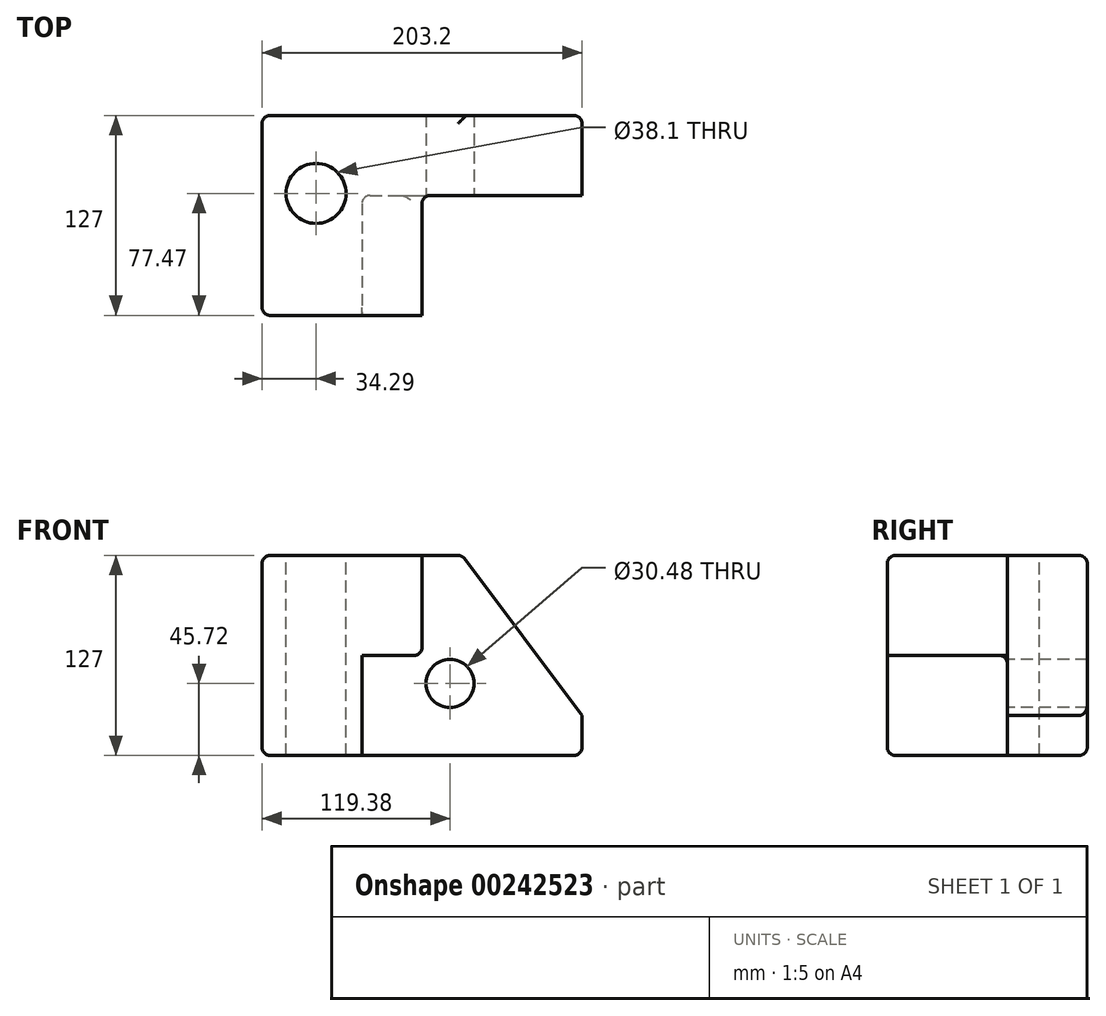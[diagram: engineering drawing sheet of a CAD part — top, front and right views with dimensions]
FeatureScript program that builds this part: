
annotation { "Feature Type Name" : "Feature", "Feature Type Description" : "" }
export const myFeature = defineFeature(function(context is Context, id is Id, definition is map)
    precondition{}
    {
        {
            var Q0;
            Q0=qCreatedBy(makeId("Front.planeOp"),FACE);
            var sketch = newSketch(context, id + "F0", { "sketchPlane" : qUnion([Q0])});
            skLineSegment(sketch, "E0.bottom", {"start": v(-101.6, 63.5) * mm, "end": v(101.6, 63.5) * mm});
            skLineSegment(sketch, "E0.top", {"start": v(-101.6, -63.5) * mm, "end": v(101.6, -63.5) * mm});
            skLineSegment(sketch, "E0.left", {"start": v(-101.6, 63.5) * mm, "end": v(-101.6, -63.5) * mm});
            skLineSegment(sketch, "E0.right", {"start": v(101.6, 63.5) * mm, "end": v(101.6, -63.5) * mm});
            skPoint(sketch, "E0.middle", {"position": v(0, 0) * mm});
            skSolve(sketch);
        }
        {
            var Q0;
            Q0=makeQuery(id+"F0.imprint","IMPRINT",FACE,{"disambiguationData":[TD([[makeQuery(id+"F0.imprint","IMPRINT",EDGE,{"derivedFrom":sQuery(id+"F0.wireOp",EDGE,"E0.bottom")}),-1.0]])]});
            extrude(context, id + "F1", {"entities" : qUnion([Q0]), "depth" : 127 * mm});
        }
        {
            var Q0;
            Q0=makeQuery(id+"F1.opExtrude","CAP_FACE",FACE,{"disambiguationData":[OSD([sQuery(id+"F0.wireOp",EDGE,"E0.bottom"),sQuery(id+"F0.wireOp",EDGE,"E0.top"),sQuery(id+"F0.wireOp",EDGE,"E0.left"),sQuery(id+"F0.wireOp",EDGE,"E0.right")])],"isStart":false});
            var sketch = newSketch(context, id + "F2", { "sketchPlane" : qUnion([Q0])});
            skLineSegment(sketch, "E1", {"start": v(-101.6, -63.5) * mm, "end": v(-38.1, -63.5) * mm});
            skLineSegment(sketch, "E2", {"start": v(-38.1, -63.5) * mm, "end": v(-38.1, 0) * mm});
            skLineSegment(sketch, "E3", {"start": v(-101.6, 63.5) * mm, "end": v(0, 63.5) * mm});
            skLineSegment(sketch, "E4", {"start": v(-38.1, 0) * mm, "end": v(0, 0) * mm});
            skLineSegment(sketch, "E5", {"start": v(0, 63.5) * mm, "end": v(0, 0) * mm});
            skLineSegment(sketch, "E6", {"start": v(-101.6, 63.5) * mm, "end": v(-101.6, -63.5) * mm});
            skSolve(sketch);
        }
        {
            var Q0;
            {var subQ3=sQuery(id+"F2.wireOp",EDGE,"E2");Q0=makeQuery(id+"F2.imprint","IMPRINT",FACE,{"disambiguationData":[TD([[makeQuery(id+"F2.imprint","IMPRINT",EDGE,{"derivedFrom":subQ3}),-1.0]])]});}
            extrude(context, id + "F3", {"entities" : qUnion([Q0]), "operationType" : NewBodyOperationType.REMOVE, "oppositeDirection" : true, "depth" : 76.2 * mm});
        }
        {
            var Q0;
            Q0=makeQuery(id+"F1.opExtrude","SWEPT_EDGE",EDGE,{"disambiguationData":[OSD([sQuery(id+"F0.wireOp",EDGE,"E0.bottom"),sQuery(id+"F0.wireOp",EDGE,"E0.right")])]});
            chamfer(context, id + "F4", {"entities" : qUnion([Q0]), "chamferType" : ChamferType.TWO_OFFSETS, "width1" : 76.2 * mm, "oppositeDirection" : false, "width2" : 101.6 * mm, "tangentPropagation" : true});
        }
        {
            var Q0;
            Q0=makeQuery(id+"F1.opExtrude","CAP_EDGE",EDGE,{"disambiguationData":[OSD([sQuery(id+"F0.wireOp",EDGE,"E0.bottom")])],"isStart":false});
            var Q1;
            Q1=makeQuery(id+"F3.boolean.opBoolean","COPY",EDGE,{"derivedFrom":makeQuery(id+"F3.opExtrude","SWEPT_EDGE",EDGE,{"disambiguationData":[OSD([sQuery(id+"F0.wireOp",EDGE,"E0.bottom"),sQuery(id+"F2.wireOp",EDGE,"E3"),sQuery(id+"F2.wireOp",EDGE,"E5")])]})});
            var Q2;
            Q2=makeQuery(id+"F3.boolean.opBoolean","COPY",EDGE,{"derivedFrom":makeQuery(id+"F3.opExtrude","CAP_EDGE",EDGE,{"disambiguationData":[OSD([sQuery(id+"F2.wireOp",EDGE,"E5")])],"isStart":true})});
            var Q3;
            Q3=makeQuery(id+"F1.opExtrude","SWEPT_EDGE",EDGE,{"disambiguationData":[OSD([sQuery(id+"F0.wireOp",EDGE,"E0.bottom"),sQuery(id+"F0.wireOp",EDGE,"E0.left")])]});
            var Q4;
            Q4=makeQuery(id+"F1.opExtrude","CAP_EDGE",EDGE,{"disambiguationData":[OSD([sQuery(id+"F0.wireOp",EDGE,"E0.bottom")])],"isStart":true});
            var Q5;
            Q5=makeQuery(id+"F3.boolean.opBoolean","COPY",EDGE,{"derivedFrom":makeQuery(id+"F3.opExtrude","CAP_EDGE",EDGE,{"disambiguationData":[OSD([sQuery(id+"F0.wireOp",EDGE,"E0.bottom")])],"isStart":false})});
            var Q6;
            {var subQ0=sQuery(id+"F0.wireOp",EDGE,"E0.bottom");Q6=makeQuery(id+"F4.opChamfer","BLEND_EDGE",EDGE,{"blendedFrom":[makeQuery(id+"F1.opExtrude","SWEPT_EDGE",EDGE,{"disambiguationData":[OSD([subQ0,sQuery(id+"F0.wireOp",EDGE,"E0.right")])]}),makeQuery(id+"F1.opExtrude","SWEPT_FACE",FACE,{"disambiguationData":[OSD([subQ0])]})],"blendedInto":[makeQuery(id+"F1.opExtrude","SWEPT_FACE",FACE,{"disambiguationData":[OSD([subQ0])]})]});}
            var Q7;
            Q7=makeQuery(id+"F3.boolean.opBoolean","COPY",EDGE,{"derivedFrom":makeQuery(id+"F3.opExtrude","CAP_EDGE",EDGE,{"disambiguationData":[OSD([sQuery(id+"F2.wireOp",EDGE,"E5")])],"isStart":false})});
            var Q8;
            Q8=makeQuery(id+"F3.boolean.opBoolean","COPY",EDGE,{"derivedFrom":makeQuery(id+"F3.opExtrude","SWEPT_EDGE",EDGE,{"disambiguationData":[OSD([sQuery(id+"F2.wireOp",EDGE,"E4"),sQuery(id+"F2.wireOp",EDGE,"E5")])]})});
            var Q9;
            Q9=makeQuery(id+"F3.boolean.opBoolean","COPY",EDGE,{"derivedFrom":makeQuery(id+"F3.opExtrude","CAP_EDGE",EDGE,{"disambiguationData":[OSD([sQuery(id+"F2.wireOp",EDGE,"E4")])],"isStart":true})});
            var Q10;
            Q10=makeQuery(id+"F3.boolean.opBoolean","COPY",EDGE,{"derivedFrom":makeQuery(id+"F3.opExtrude","CAP_EDGE",EDGE,{"disambiguationData":[OSD([sQuery(id+"F2.wireOp",EDGE,"E2")])],"isStart":true})});
            var Q11;
            Q11=makeQuery(id+"F1.opExtrude","CAP_EDGE",EDGE,{"disambiguationData":[OSD([sQuery(id+"F0.wireOp",EDGE,"E0.left")])],"isStart":false});
            var Q12;
            Q12=makeQuery(id+"F3.boolean.opBoolean","COPY",EDGE,{"derivedFrom":makeQuery(id+"F3.opExtrude","CAP_EDGE",EDGE,{"disambiguationData":[OSD([sQuery(id+"F2.wireOp",EDGE,"E2")])],"isStart":false})});
            var Q13;
            Q13=makeQuery(id+"F1.opExtrude","CAP_EDGE",EDGE,{"disambiguationData":[OSD([sQuery(id+"F0.wireOp",EDGE,"E0.top")])],"isStart":false});
            var Q14;
            Q14=makeQuery(id+"F3.boolean.opBoolean","COPY",EDGE,{"derivedFrom":makeQuery(id+"F3.opExtrude","SWEPT_EDGE",EDGE,{"disambiguationData":[OSD([sQuery(id+"F0.wireOp",EDGE,"E0.top"),sQuery(id+"F2.wireOp",EDGE,"E1"),sQuery(id+"F2.wireOp",EDGE,"E2")])]})});
            var Q15;
            Q15=makeQuery(id+"F1.opExtrude","SWEPT_EDGE",EDGE,{"disambiguationData":[OSD([sQuery(id+"F0.wireOp",EDGE,"E0.top"),sQuery(id+"F0.wireOp",EDGE,"E0.right")])]});
            fillet(context, id + "F5", {"entities" : qUnion([Q0, Q1, Q2, Q3, Q4, Q5, Q6, Q7, Q8, Q9, Q10, Q11, Q12, Q13, Q14, Q15]), "radius" : 5.08 * mm, "tangentPropagation" : true, "allowEdgeOverflow" : false});
        }
        {
            var Q0;
            Q0=makeQuery(id+"F3.boolean.opBoolean","COPY",FACE,{"derivedFrom":makeQuery(id+"F3.opExtrude","CAP_FACE",FACE,{"disambiguationData":[OSD([sQuery(id+"F0.wireOp",EDGE,"E0.bottom"),sQuery(id+"F0.wireOp",EDGE,"E0.top"),sQuery(id+"F0.wireOp",EDGE,"E0.right"),sQuery(id+"F2.wireOp",EDGE,"E2"),sQuery(id+"F2.wireOp",EDGE,"E4"),sQuery(id+"F2.wireOp",EDGE,"E5")])],"isStart":false})});
            var sketch = newSketch(context, id + "F6", { "sketchPlane" : qUnion([Q0])});
            skCircle(sketch, "E7", {"center": v(17.78, -17.78) * mm, "radius": 15.24 * mm});
            skSolve(sketch);
        }
        {
            var Q0;
            Q0=makeQuery(id+"F6.imprint","IMPRINT",FACE,{"disambiguationData":[TD([[makeQuery(id+"F6.imprint","IMPRINT",EDGE,{"derivedFrom":sQuery(id+"F6.wireOp",EDGE,"E7")}),1.0]])]});
            var Q1;
            Q1=sQuery(id+"F6.wireOp",EDGE,"E7");
            extrude(context, id + "F7", {"entities" : qUnion([Q0]), "operationType" : NewBodyOperationType.REMOVE, "surfaceEntities" : qUnion([Q1]), "oppositeDirection" : true, "depth" : 50.8 * mm});
        }
        {
            var Q0;
            Q0=makeQuery(id+"F1.opExtrude","SWEPT_FACE",FACE,{"disambiguationData":[OSD([sQuery(id+"F0.wireOp",EDGE,"E0.bottom")])]});
            var sketch = newSketch(context, id + "F8", { "sketchPlane" : qUnion([Q0])});
            skCircle(sketch, "E8", {"center": v(-67.31, -49.53) * mm, "radius": 19.05 * mm});
            skSolve(sketch);
        }
        {
            var Q0;
            Q0=makeQuery(id+"F8.imprint","IMPRINT",FACE,{"disambiguationData":[TD([[makeQuery(id+"F8.imprint","IMPRINT",EDGE,{"derivedFrom":sQuery(id+"F8.wireOp",EDGE,"E8")}),1.0]])]});
            var Q1;
            Q1=sQuery(id+"F8.wireOp",EDGE,"E8");
            extrude(context, id + "F9", {"entities" : qUnion([Q0]), "operationType" : NewBodyOperationType.REMOVE, "surfaceEntities" : qUnion([Q1]), "oppositeDirection" : true, "depth" : 127 * mm});
        }
        {
            var Q0;
            Q0=makeQuery(id+"F1.opExtrude","CAP_EDGE",EDGE,{"disambiguationData":[OSD([sQuery(id+"F0.wireOp",EDGE,"E0.top")])],"isStart":true});
            var Q1;
            Q1=makeQuery(id+"F1.opExtrude","SWEPT_EDGE",EDGE,{"disambiguationData":[OSD([sQuery(id+"F0.wireOp",EDGE,"E0.top"),sQuery(id+"F0.wireOp",EDGE,"E0.left")])]});
            var Q2;
            Q2=makeQuery(id+"F1.opExtrude","CAP_EDGE",EDGE,{"disambiguationData":[OSD([sQuery(id+"F0.wireOp",EDGE,"E0.left")])],"isStart":true});
            fillet(context, id + "F10", {"entities" : qUnion([Q0, Q1, Q2]), "radius" : 5.08 * mm, "tangentPropagation" : true, "allowEdgeOverflow" : false});
        }
    });
